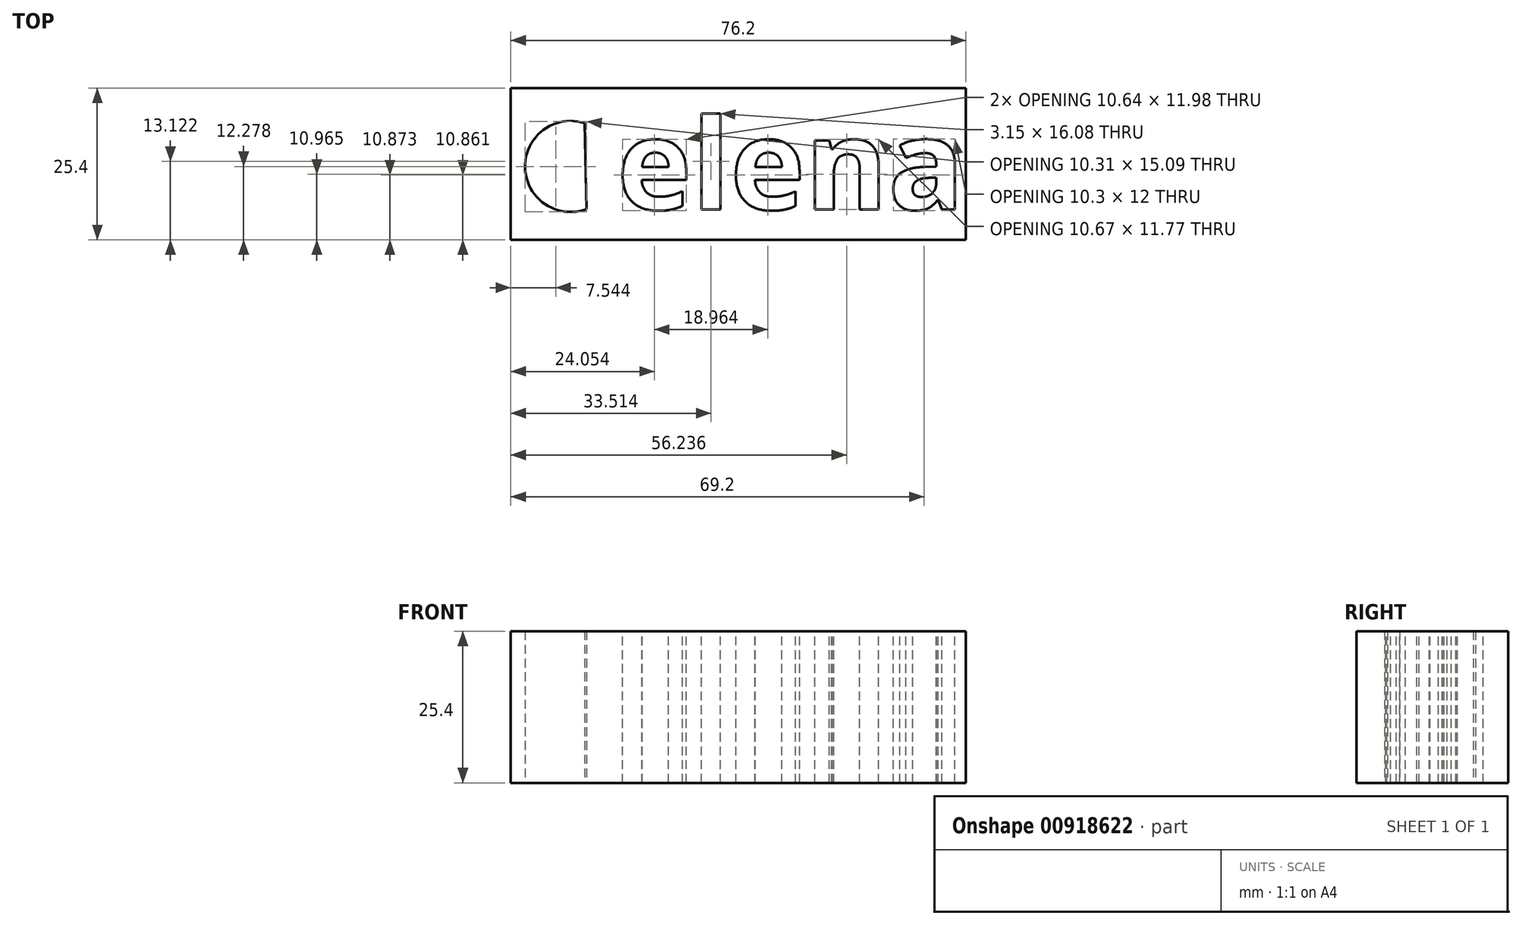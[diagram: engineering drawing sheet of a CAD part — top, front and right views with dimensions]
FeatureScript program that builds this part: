
annotation { "Feature Type Name" : "Feature", "Feature Type Description" : "" }
export const myFeature = defineFeature(function(context is Context, id is Id, definition is map)
    precondition{}
    {
        {
            var Q0;
            Q0=qCreatedBy(makeId("Top.planeOp"),FACE);
            var sketch = newSketch(context, id + "F0", { "sketchPlane" : qUnion([Q0])});
            skLineSegment(sketch, "E0.bottom", {"start": v(0, 0) * mm, "end": v(76.2, 0) * mm});
            skLineSegment(sketch, "E0.top", {"start": v(0, -25.4) * mm, "end": v(76.2, -25.4) * mm});
            skLineSegment(sketch, "E0.left", {"start": v(0, 0) * mm, "end": v(0, -25.4) * mm});
            skLineSegment(sketch, "E0.right", {"start": v(76.2, 0) * mm, "end": v(76.2, -25.4) * mm});
            skSolve(sketch);
        }
        {
            var Q0;
            Q0=makeQuery(id+"F0.imprint","IMPRINT",FACE,{"disambiguationData":[TD([[makeQuery(id+"F0.imprint","IMPRINT",EDGE,{"derivedFrom":sQuery(id+"F0.wireOp",EDGE,"E0.bottom")}),-1.0]])]});
            extrude(context, id + "F1", {"entities" : qUnion([Q0]), "depth" : 25.4 * mm, "offsetDistance" : 25.4 * mm});
        }
        {
            var Q0;
            Q0=makeQuery(id+"F1.opExtrude","CAP_FACE",FACE,{"disambiguationData":[OSD([sQuery(id+"F0.wireOp",EDGE,"E0.bottom"),sQuery(id+"F0.wireOp",EDGE,"E0.top"),sQuery(id+"F0.wireOp",EDGE,"E0.left"),sQuery(id+"F0.wireOp",EDGE,"E0.right")])],"isStart":false});
            var sketch = newSketch(context, id + "F2", { "sketchPlane" : qUnion([Q0])});
            skText(sketch, "E1", { "text": "elena", "fontName": "OpenSans-Bold.ttf"});
            const initialGuessF2  = {"E1": [0.01778, -0.02032, 1, 0, 0.01524]};
            skSetInitialGuess(sketch, initialGuessF2);
            skSolve(sketch);
        }
        {
            var Q0;
            Q0=qCreatedBy(makeId("Top.planeOp"),FACE);
            var sketch = newSketch(context, id + "F3", { "sketchPlane" : qUnion([Q0])});
            skArc(sketch, "E2", {"start": v(12.36, -5.85) * mm, "mid": v(2.39, -13.28) * mm, "end": v(12.7, -20.22) * mm});
            skLineSegment(sketch, "E3", {"start": v(12.36, -5.85) * mm, "end": v(12.7, -20.22) * mm});
            skSolve(sketch);
        }
        {
            var Q0;
            Q0 = qSketchRegion(id + "F3", true);
            extrude(context, id + "F4", {"entities" : qUnion([Q0]), "operationType" : NewBodyOperationType.REMOVE, "depth" : 25.4 * mm, "offsetDistance" : 25.4 * mm});
        }
        {
            var Q0;
            Q0 = qSketchRegion(id + "F2", true);
            extrude(context, id + "F5", {"entities" : qUnion([Q0]), "operationType" : NewBodyOperationType.REMOVE, "oppositeDirection" : true, "depth" : 25.4 * mm, "offsetDistance" : 25.4 * mm});
        }
    });
